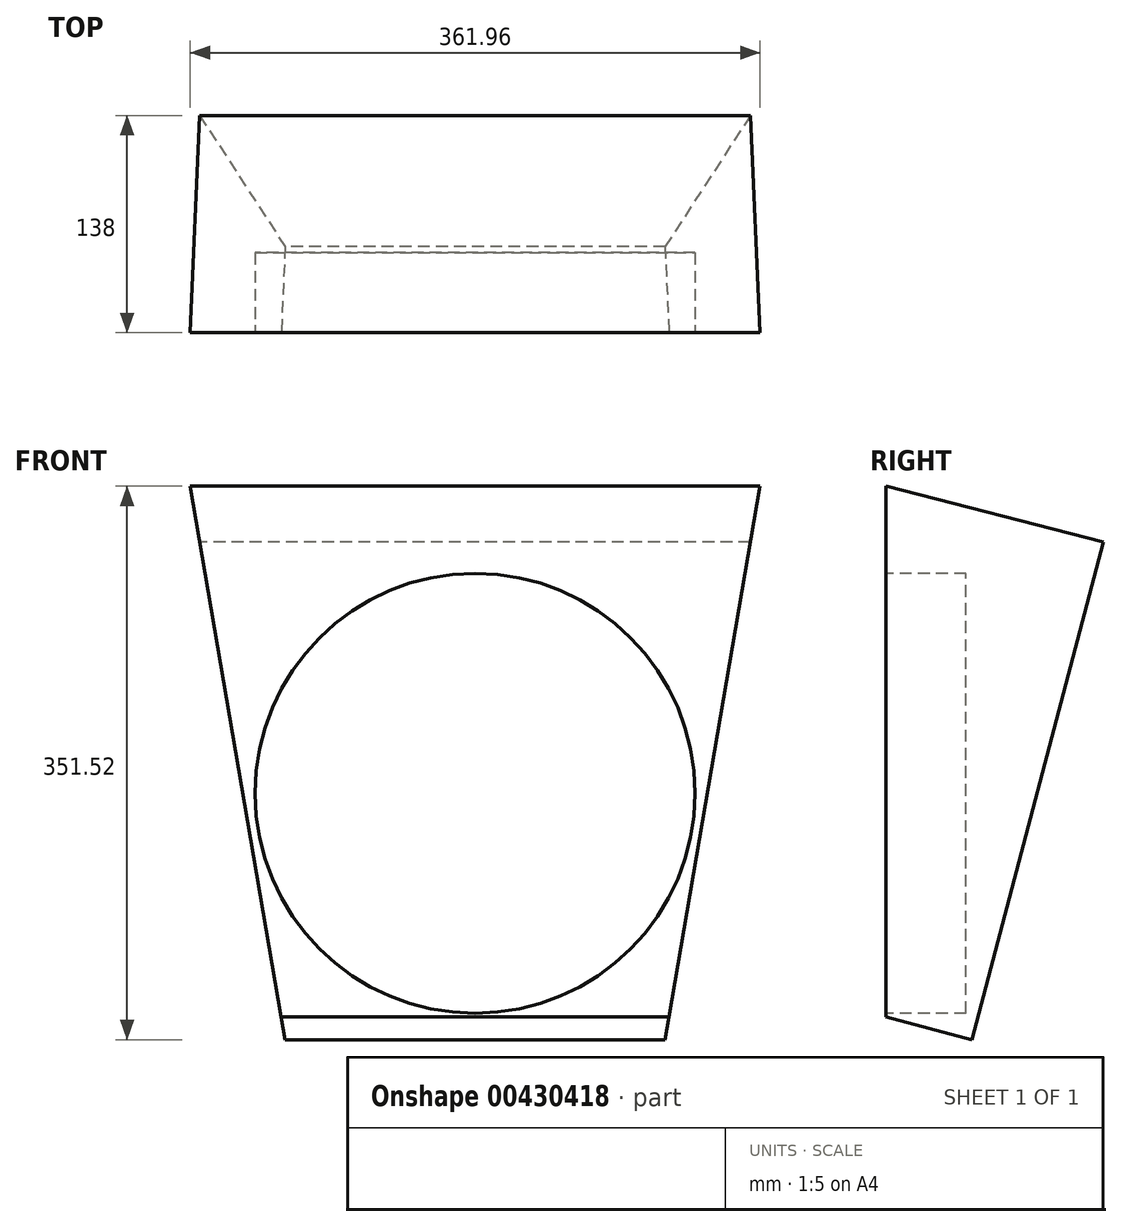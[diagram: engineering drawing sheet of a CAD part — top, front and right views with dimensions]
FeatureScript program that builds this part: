
annotation { "Feature Type Name" : "Feature", "Feature Type Description" : "" }
export const myFeature = defineFeature(function(context is Context, id is Id, definition is map)
    precondition{}
    {
        {
            var Q0;
            Q0=qCreatedBy(makeId("Right.planeOp"),FACE);
            var sketch = newSketch(context, id + "F0", { "sketchPlane" : qUnion([Q0])});
            skLineSegment(sketch, "E0.0", {"start": v(-41.3, 234.68) * mm, "end": v(96.7, 199.12) * mm});
            skLineSegment(sketch, "E0.1", {"start": v(-41.3, 234.68) * mm, "end": v(-41.3, -100.43) * mm});
            skLineSegment(sketch, "E0.2", {"start": v(96.7, 199.12) * mm, "end": v(14.07, -114.2) * mm});
            skLineSegment(sketch, "E0.3", {"start": v(13.37, -116.83) * mm, "end": v(-41.79, -102.28) * mm});
            skLineSegment(sketch, "E1", {"start": v(-41.3, -100.43) * mm, "end": v(-41.3, -102.41) * mm});
            skLineSegment(sketch, "E2", {"start": v(14.07, -114.2) * mm, "end": v(13.37, -116.83) * mm});
            skSolve(sketch);
        }
        {
            var Q0;
            Q0 = qSketchRegion(id + "F0", true);
            extrude(context, id + "F1", {"entities" : qUnion([Q0]), "depth" : 361.95 * mm, "offsetDistance" : 25.4 * mm, "symmetric" : true});
        }
        {
            var Q0;
            Q0=makeQuery(id+"F1.opExtrude","SWEPT_BODY",BODY,{"disambiguationData":[OSD([sQuery(id+"F0.wireOp",EDGE,"E0.0"),sQuery(id+"F0.wireOp",EDGE,"E0.1"),sQuery(id+"F0.wireOp",EDGE,"E0.2"),sQuery(id+"F0.wireOp",EDGE,"E0.3"),sQuery(id+"F0.wireOp",EDGE,"E1"),sQuery(id+"F0.wireOp",EDGE,"E2")])]});
            transform(context, id + "F2", {"entities" : qUnion([Q0]), "transformType" : TransformType.TRANSLATION_3D, "dx" : 0 * mm, "dy" : 41.3 * mm, "dz" : -26.54 * mm, "makeCopy" : false});
        }
        {
            var Q0;
            Q0=makeQuery(id+"F1.opExtrude","SWEPT_FACE",FACE,{"disambiguationData":[OSD([sQuery(id+"F0.wireOp",EDGE,"E0.1"),sQuery(id+"F0.wireOp",EDGE,"E1")])]});
            var sketch = newSketch(context, id + "F3", { "sketchPlane" : qUnion([Q0])});
            skPoint(sketch, "E3.1", {"position": v(180.98, 208.15) * mm});
            skLineSegment(sketch, "E4.1", {"start": v(120.65, -143.37) * mm, "end": v(124.62, -107.34) * mm});
            skLineSegment(sketch, "E5", {"start": v(120.65, -143.37) * mm, "end": v(180.98, 208.15) * mm});
            skLineSegment(sketch, "E6", {"start": v(120.65, -143.37) * mm, "end": v(410.7, -143.37) * mm});
            skLineSegment(sketch, "E7", {"start": v(180.98, 208.15) * mm, "end": v(410.7, -143.37) * mm});
            skLineSegment(sketch, "E8", {"start": v(0, 352.04) * mm, "end": v(0, -210.61) * mm, "construction": true});
            skLineSegment(sketch, "E9.MirrorCS", {"start": v(-120.65, -143.37) * mm, "end": v(-124.62, -107.34) * mm});
            skLineSegment(sketch, "E10.MirrorCS", {"start": v(-120.65, -143.37) * mm, "end": v(-410.7, -143.37) * mm});
            skLineSegment(sketch, "E11.MirrorCS", {"start": v(-180.97, 208.15) * mm, "end": v(-410.7, -143.37) * mm});
            skPoint(sketch, "E12.MirrorP", {"position": v(-180.98, 208.15) * mm});
            skLineSegment(sketch, "E13.MirrorCS", {"start": v(-120.65, -143.37) * mm, "end": v(-180.98, 208.15) * mm});
            skSolve(sketch);
        }
        {
            var Q0;
            Q0 = qSketchRegion(id + "F3", true);
            extrude(context, id + "F4", {"entities" : qUnion([Q0]), "operationType" : NewBodyOperationType.REMOVE, "oppositeDirection" : true, "depth" : 304.8 * mm, "offsetDistance" : 25.4 * mm, "symmetric" : true});
        }
        {
            var Q0;
            Q0=qCreatedBy(makeId("Front.planeOp"),FACE);
            var sketch = newSketch(context, id + "F5", { "sketchPlane" : qUnion([Q0])});
            skCircle(sketch, "E14", {"center": v(0, 13.13) * mm, "radius": 139.7 * mm});
            skSolve(sketch);
        }
        {
            var Q0;
            Q0 = qSketchRegion(id + "F5", true);
            extrude(context, id + "F6", {"entities" : qUnion([Q0]), "oppositeDirection" : true, "depth" : 50.8 * mm, "offsetDistance" : 25.4 * mm});
        }
    });
